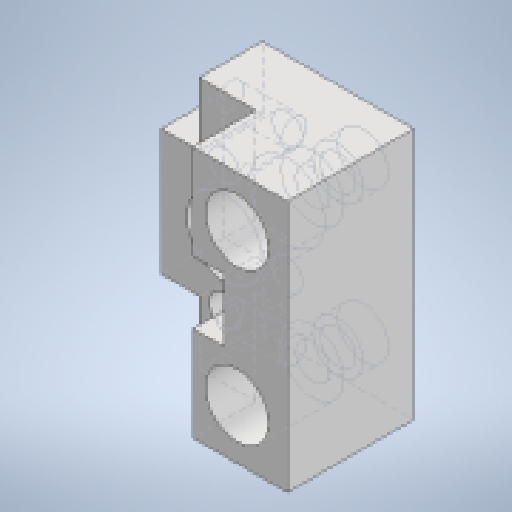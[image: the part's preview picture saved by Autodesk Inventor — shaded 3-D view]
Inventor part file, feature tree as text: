
AUTODESK INVENTOR PART (.ipt)
format: ipt  version: 2023 (Build 270158000, 158)  size: 246,272 bytes
history: native  units: mm
features: extrude x7, sketch x7, thread x2
ambient origin geometry x8: Origin, YZ Plane, XZ Plane, XY Plane, X Axis, Y Axis, Z Axis, Center Point
bodies: Solid1 (feature_tree)
feature tree (16):
  extrude  "Extrusion1"  Depth=10.0mm
  extrude  "Extrusion2"  Depth=10.0mm
  extrude  "Extrusion6"  Depth=5.0mm
  extrude  "Extrusion7"  Depth=2.4mm
  extrude  "Extrusion8"  Depth=5.0mm TaperAngle=0.0deg
  extrude  "Extrusion9"  Depth=4.0mm
  extrude  "Extrusion10"  Depth=4.0mm
  thread  "Thread1"  [1 undecoded]
  thread  "Thread2"  [1 undecoded]
  sketch  "Sketch1"  dims[d0=10.0mm d1=10.0mm]
  sketch  "Sketch2"  dims[d2=10.0mm d3=10.0mm]
  sketch  "Sketch7"  dims[d4=5.0mm d5=5.0mm]
  sketch  "Sketch8"  dims[d6=2.4mm d7=2.4mm]
  sketch  "Sketch9"  dims[d8=6.0mm d9=5.0mm d10=0.0mm]
  sketch  "Sketch10"  dims[d17=1.0mm d18=0.0mm d34=4.0mm]
  sketch  "Sketch11"  dims[d35=4.0mm d36=4.0mm d37=4.0mm d38=5.0mm d39=5.0mm d40=2.75mm d41=2.75mm d42=5.0mm d43=0.0mm d44=7.5mm d45=7.5mm d46=7.5mm d47=7.5mm d48=5.0mm d49=5.0mm d50=0.0mm d51=4.0mm d52=4.0mm d53=2.0mm d54=0.0mm d55=5.0mm d56=3.0mm d57=5.0mm d58=5.0mm d59=3.0mm d60=10.0mm d61=0.0mm d62=2.5mm d63=2.5mm d64=2.05mm d65=2.5mm d66=2.5mm d67=2.05mm d68=5.0mm d69=0.0mm d70=5.0mm d71=0.0mm d72=5.0mm d73=0.0mm]
note: 2 required parameter values undecoded (feature->parameter linkage not recoverable at this tier; creation-order binding heuristic only, values carry confidence <= 0.55)
